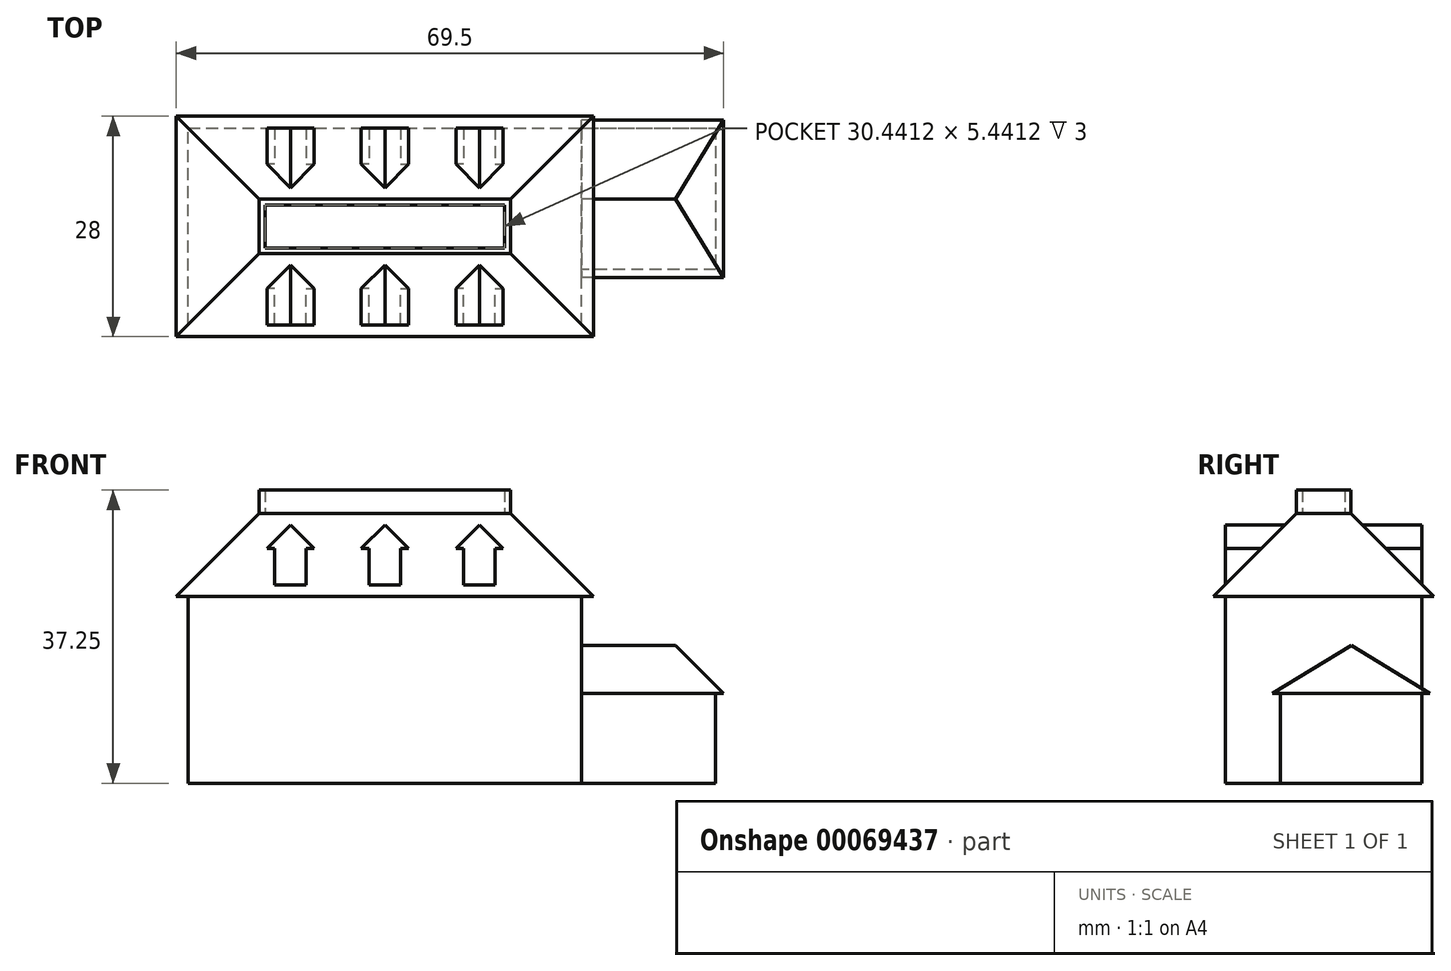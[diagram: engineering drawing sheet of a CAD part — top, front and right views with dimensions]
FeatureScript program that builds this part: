
annotation { "Feature Type Name" : "Feature", "Feature Type Description" : "" }
export const myFeature = defineFeature(function(context is Context, id is Id, definition is map)
    precondition{}
    {
        {
            var Q0;
            Q0=qCreatedBy(makeId("Top.planeOp"),FACE);
            var sketch = newSketch(context, id + "F0", { "sketchPlane" : qUnion([Q0])});
            skLineSegment(sketch, "E0.rect.bottom", {"start": v(25, -12.5) * mm, "end": v(-25, -12.5) * mm});
            skLineSegment(sketch, "E0.rect.top", {"start": v(25, 12.5) * mm, "end": v(-25, 12.5) * mm});
            skLineSegment(sketch, "E0.rect.left", {"start": v(25, -12.5) * mm, "end": v(25, 12.5) * mm, "construction": true});
            skLineSegment(sketch, "E0.rect.right", {"start": v(-25, -12.5) * mm, "end": v(-25, 12.5) * mm});
            skPoint(sketch, "E0.rect.middle", {"position": v(0, 0) * mm});
            skLineSegment(sketch, "E1", {"start": v(25, 12.5) * mm, "end": v(42, 12.5) * mm});
            skLineSegment(sketch, "E2", {"start": v(42, 12.5) * mm, "end": v(42, -5.5) * mm});
            skLineSegment(sketch, "E3", {"start": v(42, -5.5) * mm, "end": v(25, -5.5) * mm});
            skLineSegment(sketch, "E4", {"start": v(25, -12.5) * mm, "end": v(25, -5.5) * mm, "construction": true});
            skLineSegment(sketch, "E5", {"start": v(25, -12.5) * mm, "end": v(25, -5.5) * mm});
            skSolve(sketch);
        }
        {
            var Q0;
            Q0=makeQuery(id+"F0.imprint","IMPRINT",FACE,{"disambiguationData":[TD([[makeQuery(id+"F0.imprint","IMPRINT",EDGE,{"derivedFrom":sQuery(id+"F0.wireOp",EDGE,"E0.rect.bottom")}),-1.0]])]});
            extrude(context, id + "F1", {"entities" : qUnion([Q0]), "depth" : 11.43 * mm});
        }
        {
            var Q0;
            Q0=makeQuery(id+"F1.opExtrude","CAP_FACE",FACE,{"disambiguationData":[OSD([sQuery(id+"F0.wireOp",EDGE,"E0.rect.bottom"),sQuery(id+"F0.wireOp",EDGE,"E0.rect.top"),sQuery(id+"F0.wireOp",EDGE,"E0.rect.right"),sQuery(id+"F0.wireOp",EDGE,"E1"),sQuery(id+"F0.wireOp",EDGE,"E2"),sQuery(id+"F0.wireOp",EDGE,"E3"),sQuery(id+"F0.wireOp",EDGE,"E5")])],"isStart":false});
            var sketch = newSketch(context, id + "F2", { "sketchPlane" : qUnion([Q0])});
            skLineSegment(sketch, "E6.0", {"start": v(25, -12.5) * mm, "end": v(-25, -12.5) * mm});
            skLineSegment(sketch, "E6.1", {"start": v(25, 12.5) * mm, "end": v(-25, 12.5) * mm});
            skLineSegment(sketch, "E6.2", {"start": v(25, -12.5) * mm, "end": v(25, 12.5) * mm});
            skLineSegment(sketch, "E6.3", {"start": v(-25, -12.5) * mm, "end": v(-25, 12.5) * mm});
            skPoint(sketch, "E6.4", {"position": v(0, 0) * mm});
            skLineSegment(sketch, "E6.8", {"start": v(25, -12.5) * mm, "end": v(25, -5.5) * mm});
            skLineSegment(sketch, "E6.9", {"start": v(25, -12.5) * mm, "end": v(25, -5.5) * mm});
            skPoint(sketch, "E6.7.end.orphan", {"position": v(25, -5.5) * mm});
            skPoint(sketch, "E6.7.start.orphan", {"position": v(42, -5.5) * mm});
            skPoint(sketch, "E6.6.end.orphan", {"position": v(42, -5.5) * mm});
            skPoint(sketch, "E6.6.start.orphan", {"position": v(42, 12.5) * mm});
            skPoint(sketch, "E6.5.end.orphan", {"position": v(42, 12.5) * mm});
            skPoint(sketch, "E6.5.start.orphan", {"position": v(25, 12.5) * mm});
            skSolve(sketch);
        }
        {
            var Q0;
            Q0=makeQuery(id+"F2.imprint","IMPRINT",FACE,{"disambiguationData":[TD([[makeQuery(id+"F2.imprint","IMPRINT",EDGE,{"derivedFrom":sQuery(id+"F2.wireOp",EDGE,"E6.0")}),-1.0]])]});
            extrude(context, id + "F3", {"entities" : qUnion([Q0]), "operationType" : NewBodyOperationType.ADD, "depth" : 12.29 * mm});
        }
        {
            var Q0;
            Q0=makeQuery(id+"F3.opExtrude","CAP_FACE",FACE,{"disambiguationData":[OSD([sQuery(id+"F2.wireOp",EDGE,"E6.0"),sQuery(id+"F2.wireOp",EDGE,"E6.1"),sQuery(id+"F2.wireOp",EDGE,"E6.2"),sQuery(id+"F2.wireOp",EDGE,"E6.3"),sQuery(id+"F2.wireOp",EDGE,"E6.9")])],"isStart":false});
            var sketch = newSketch(context, id + "F4", { "sketchPlane" : qUnion([Q0])});
            skLineSegment(sketch, "E7.0", {"start": v(25, -12.5) * mm, "end": v(-25, -12.5) * mm, "construction": true});
            skLineSegment(sketch, "E7.1", {"start": v(25, 12.5) * mm, "end": v(-25, 12.5) * mm, "construction": true});
            skLineSegment(sketch, "E7.2", {"start": v(25, -12.5) * mm, "end": v(25, 12.5) * mm, "construction": true});
            skLineSegment(sketch, "E7.3", {"start": v(-25, -12.5) * mm, "end": v(-25, 12.5) * mm, "construction": true});
            skPoint(sketch, "E7.4", {"position": v(0, 0) * mm});
            skLineSegment(sketch, "E7.5", {"start": v(25, -12.5) * mm, "end": v(25, -5.5) * mm});
            skLineSegment(sketch, "E7.6", {"start": v(25, -12.5) * mm, "end": v(25, -5.5) * mm});
            skPoint(sketch, "E7.7", {"position": v(25, -5.5) * mm});
            skPoint(sketch, "E7.8", {"position": v(42, -5.5) * mm});
            skPoint(sketch, "E7.9", {"position": v(42, -5.5) * mm});
            skPoint(sketch, "E7.10", {"position": v(42, 12.5) * mm});
            skPoint(sketch, "E7.11", {"position": v(42, 12.5) * mm});
            skPoint(sketch, "E7.12", {"position": v(25, 12.5) * mm});
            skLineSegment(sketch, "E8.0", {"start": v(26.5, 14) * mm, "end": v(-26.5, 14) * mm});
            skLineSegment(sketch, "E8.1", {"start": v(26.5, -14) * mm, "end": v(26.5, 14) * mm});
            skLineSegment(sketch, "E8.2", {"start": v(26.5, -14) * mm, "end": v(-26.5, -14) * mm});
            skLineSegment(sketch, "E8.3", {"start": v(-26.5, -14) * mm, "end": v(-26.5, 14) * mm});
            skSolve(sketch);
        }
        {
            var Q0;
            Q0 = qSketchRegion(id + "F4", true);
            var Q1;
            Q1=sQuery(id+"F4.wireOp",EDGE,"E8.0");
            extrude(context, id + "F5", {"entities" : qUnion([Q0]), "operationType" : NewBodyOperationType.ADD, "surfaceEntities" : qUnion([Q1]), "depth" : 10.54 * mm, "hasDraft" : true, "draftAngle" : 45 * degree, "draftPullDirection" : true});
        }
        {
            var Q0;
            Q0=makeQuery(id+"F3.boolean.opBoolean","MERGE",FACE,{"derivedFrom":[makeQuery(id+"F1.opExtrude","SWEPT_FACE",FACE,{"disambiguationData":[OSD([sQuery(id+"F0.wireOp",EDGE,"E0.rect.bottom")])]}),makeQuery(id+"F3.opExtrude","SWEPT_FACE",FACE,{"disambiguationData":[OSD([sQuery(id+"F2.wireOp",EDGE,"E6.0")])]})]});
            var sketch = newSketch(context, id + "F6", { "sketchPlane" : qUnion([Q0])});
            skLineSegment(sketch, "E9", {"start": v(25, 25.22) * mm, "end": v(-25, 25.22) * mm, "construction": true});
            skLineSegment(sketch, "E10", {"start": v(-15, 29.82) * mm, "end": v(-12, 32.82) * mm});
            skLineSegment(sketch, "E11", {"start": v(-12, 32.82) * mm, "end": v(-12, 25.22) * mm, "construction": true});
            skLineSegment(sketch, "E12", {"start": v(-12, 25.22) * mm, "end": v(-14, 25.22) * mm});
            skLineSegment(sketch, "E13", {"start": v(-15, 29.82) * mm, "end": v(-14, 29.82) * mm});
            skLineSegment(sketch, "E14", {"start": v(-14, 29.82) * mm, "end": v(-14, 25.22) * mm});
            skLineSegment(sketch, "E15.MirrorCS", {"start": v(-9, 29.82) * mm, "end": v(-10, 29.82) * mm});
            skLineSegment(sketch, "E16.MirrorCS", {"start": v(-9, 29.82) * mm, "end": v(-12, 32.82) * mm});
            skLineSegment(sketch, "E17.MirrorCS", {"start": v(-10, 29.82) * mm, "end": v(-10, 25.22) * mm});
            skLineSegment(sketch, "E18.MirrorCS", {"start": v(-12, 25.22) * mm, "end": v(-10, 25.22) * mm});
            skLineSegment(sketch, "E19.1.0.0", {"start": v(0, 25.22) * mm, "end": v(2, 25.22) * mm});
            skLineSegment(sketch, "E19.1.0.1", {"start": v(2, 29.82) * mm, "end": v(2, 25.22) * mm});
            skLineSegment(sketch, "E19.1.0.2", {"start": v(-3, 29.82) * mm, "end": v(0, 32.82) * mm});
            skLineSegment(sketch, "E19.1.0.3", {"start": v(3, 29.82) * mm, "end": v(0, 32.82) * mm});
            skLineSegment(sketch, "E19.1.0.4", {"start": v(0, 32.82) * mm, "end": v(0, 25.22) * mm, "construction": true});
            skLineSegment(sketch, "E19.1.0.5", {"start": v(0, 25.22) * mm, "end": v(-2, 25.22) * mm});
            skLineSegment(sketch, "E19.1.0.6", {"start": v(-2, 29.82) * mm, "end": v(-2, 25.22) * mm});
            skLineSegment(sketch, "E19.1.0.7", {"start": v(3, 29.82) * mm, "end": v(2, 29.82) * mm});
            skLineSegment(sketch, "E19.1.0.8", {"start": v(-3, 29.82) * mm, "end": v(-2, 29.82) * mm});
            skLineSegment(sketch, "E19.2.0.0", {"start": v(12, 25.22) * mm, "end": v(14, 25.22) * mm});
            skLineSegment(sketch, "E19.2.0.1", {"start": v(14, 29.82) * mm, "end": v(14, 25.22) * mm});
            skLineSegment(sketch, "E19.2.0.2", {"start": v(9, 29.82) * mm, "end": v(12, 32.82) * mm});
            skLineSegment(sketch, "E19.2.0.3", {"start": v(15, 29.82) * mm, "end": v(12, 32.82) * mm});
            skLineSegment(sketch, "E19.2.0.4", {"start": v(12, 32.82) * mm, "end": v(12, 25.22) * mm, "construction": true});
            skLineSegment(sketch, "E19.2.0.5", {"start": v(12, 25.22) * mm, "end": v(10, 25.22) * mm});
            skLineSegment(sketch, "E19.2.0.6", {"start": v(10, 29.82) * mm, "end": v(10, 25.22) * mm});
            skLineSegment(sketch, "E19.2.0.7", {"start": v(15, 29.82) * mm, "end": v(14, 29.82) * mm});
            skLineSegment(sketch, "E19.2.0.8", {"start": v(9, 29.82) * mm, "end": v(10, 29.82) * mm});
            skLineSegment(sketch, "E19.direction1", {"start": v(-12, 25.22) * mm, "end": v(0, 25.22) * mm, "construction": true});
            skSolve(sketch);
        }
        {
            var Q0;
            Q0=makeQuery(id+"F6.imprint","IMPRINT",FACE,{"disambiguationData":[TD([[makeQuery(id+"F6.imprint","IMPRINT",EDGE,{"derivedFrom":sQuery(id+"F6.wireOp",EDGE,"E10")}),-1.0]])]});
            var Q1;
            Q1=makeQuery(id+"F6.imprint","IMPRINT",FACE,{"disambiguationData":[TD([[makeQuery(id+"F6.imprint","IMPRINT",EDGE,{"derivedFrom":sQuery(id+"F6.wireOp",EDGE,"E19.1.0.0")}),1.0]])]});
            var Q2;
            Q2=makeQuery(id+"F6.imprint","IMPRINT",FACE,{"disambiguationData":[TD([[makeQuery(id+"F6.imprint","IMPRINT",EDGE,{"derivedFrom":sQuery(id+"F6.wireOp",EDGE,"E19.2.0.0")}),1.0]])]});
            var Q3;
            Q3=makeQuery(id+"F1.opExtrude","SWEPT_BODY",BODY,{"disambiguationData":[OSD([sQuery(id+"F0.wireOp",EDGE,"E0.rect.bottom"),sQuery(id+"F0.wireOp",EDGE,"E0.rect.top"),sQuery(id+"F0.wireOp",EDGE,"E0.rect.right"),sQuery(id+"F0.wireOp",EDGE,"E1"),sQuery(id+"F0.wireOp",EDGE,"E2"),sQuery(id+"F0.wireOp",EDGE,"E3"),sQuery(id+"F0.wireOp",EDGE,"E5")])]});
            extrude(context, id + "F7", {"entities" : qUnion([Q0, Q1, Q2]), "endBound" : BoundingType.UP_TO_BODY, "oppositeDirection" : true, "endBoundEntityBody" : qUnion([Q3]), "depth" : 25 * mm});
        }
        {
            var Q0;
            Q0=makeQuery(id+"F7.opExtrude","SWEPT_BODY",BODY,{"disambiguationData":[OSD([sQuery(id+"F6.wireOp",EDGE,"E10"),sQuery(id+"F6.wireOp",EDGE,"E12"),sQuery(id+"F6.wireOp",EDGE,"E13"),sQuery(id+"F6.wireOp",EDGE,"E14"),sQuery(id+"F6.wireOp",EDGE,"E15.MirrorCS"),sQuery(id+"F6.wireOp",EDGE,"E16.MirrorCS"),sQuery(id+"F6.wireOp",EDGE,"E17.MirrorCS"),sQuery(id+"F6.wireOp",EDGE,"E18.MirrorCS")])]});
            var Q1;
            Q1=makeQuery(id+"F7.opExtrude","SWEPT_BODY",BODY,{"disambiguationData":[OSD([sQuery(id+"F6.wireOp",EDGE,"E19.1.0.0"),sQuery(id+"F6.wireOp",EDGE,"E19.1.0.1"),sQuery(id+"F6.wireOp",EDGE,"E19.1.0.2"),sQuery(id+"F6.wireOp",EDGE,"E19.1.0.3"),sQuery(id+"F6.wireOp",EDGE,"E19.1.0.5"),sQuery(id+"F6.wireOp",EDGE,"E19.1.0.6"),sQuery(id+"F6.wireOp",EDGE,"E19.1.0.7"),sQuery(id+"F6.wireOp",EDGE,"E19.1.0.8")])]});
            var Q2;
            Q2=makeQuery(id+"F7.opExtrude","SWEPT_BODY",BODY,{"disambiguationData":[OSD([sQuery(id+"F6.wireOp",EDGE,"E19.2.0.0"),sQuery(id+"F6.wireOp",EDGE,"E19.2.0.1"),sQuery(id+"F6.wireOp",EDGE,"E19.2.0.2"),sQuery(id+"F6.wireOp",EDGE,"E19.2.0.3"),sQuery(id+"F6.wireOp",EDGE,"E19.2.0.5"),sQuery(id+"F6.wireOp",EDGE,"E19.2.0.6"),sQuery(id+"F6.wireOp",EDGE,"E19.2.0.7"),sQuery(id+"F6.wireOp",EDGE,"E19.2.0.8")])]});
            var Q3;
            Q3=qCreatedBy(makeId("Front.planeOp"),FACE);
            mirror(context, id + "F8", {"operationType" : NewBodyOperationType.ADD, "entities" : qUnion([Q0, Q1, Q2]), "mirrorPlane" : qUnion([Q3])});
        }
        {
            var Q0;
            Q0=makeQuery(id+"F3.boolean.opBoolean","MERGE",FACE,{"derivedFrom":[makeQuery(id+"F1.opExtrude","SWEPT_FACE",FACE,{"disambiguationData":[OSD([sQuery(id+"F0.wireOp",EDGE,"E5")])]}),makeQuery(id+"F3.opExtrude","SWEPT_FACE",FACE,{"disambiguationData":[OSD([sQuery(id+"F2.wireOp",EDGE,"E6.2"),sQuery(id+"F2.wireOp",EDGE,"E6.9")])]})]});
            var sketch = newSketch(context, id + "F9", { "sketchPlane" : qUnion([Q0])});
            skLineSegment(sketch, "E20", {"start": v(-6.5, 11.43) * mm, "end": v(13.5, 11.43) * mm});
            skLineSegment(sketch, "E21", {"start": v(13.5, 11.43) * mm, "end": v(3.5, 17.5) * mm});
            skLineSegment(sketch, "E22", {"start": v(3.5, 17.5) * mm, "end": v(-6.5, 11.43) * mm});
            skPoint(sketch, "E23", {"position": v(3.5, 11.43) * mm});
            skSolve(sketch);
        }
        {
            var Q0;
            {var subQ0=sQuery(id+"F9.wireOp",EDGE,"E22");Q0=makeQuery(id+"F9.imprint","IMPRINT",FACE,{"disambiguationData":[TD([[makeQuery(id+"F9.imprint","IMPRINT",EDGE,{"derivedFrom":subQ0}),1.0]])]});}
            var Q1;
            {var subQ0=sQuery(id+"F9.wireOp",EDGE,"E20");var subQ3=sQuery(id+"F9.wireOp",EDGE,"E21");var subQ4=makeQuery(id+"F9.imprint","INTERSECT",VERTEX,{"derivedFrom":[subQ0,subQ3]});Q1=makeQuery(id+"F9.imprint","IMPRINT",FACE,{"disambiguationData":[TD([[makeQuery(id+"F9.imprint","IMPRINT",EDGE,{"disambiguationData":[TD([[subQ4,1.0]])],"derivedFrom":subQ0}),1.0]])]});}
            extrude(context, id + "F10", {"entities" : qUnion([Q0, Q1]), "operationType" : NewBodyOperationType.ADD, "depth" : 18 * mm});
        }
        {
            var Q0;
            Q0=makeQuery(id+"F1.opExtrude","SWEPT_FACE",FACE,{"disambiguationData":[OSD([sQuery(id+"F0.wireOp",EDGE,"E3")])]});
            var sketch = newSketch(context, id + "F11", { "sketchPlane" : qUnion([Q0])});
            skLineSegment(sketch, "E24", {"start": v(43, 17.5) * mm, "end": v(36.94, 17.5) * mm});
            skLineSegment(sketch, "E25", {"start": v(36.94, 17.5) * mm, "end": v(43, 11.43) * mm});
            skLineSegment(sketch, "E26", {"start": v(43, 11.43) * mm, "end": v(43, 17.5) * mm});
            skSolve(sketch);
        }
        {
            var Q0;
            Q0=makeQuery(id+"F11.imprint","IMPRINT",FACE,{"disambiguationData":[TD([[makeQuery(id+"F11.imprint","IMPRINT",EDGE,{"derivedFrom":sQuery(id+"F11.wireOp",EDGE,"E24")}),1.0]])]});
            extrude(context, id + "F12", {"entities" : qUnion([Q0]), "operationType" : NewBodyOperationType.REMOVE, "endBound" : BoundingType.THROUGH_ALL, "oppositeDirection" : true, "depth" : 25 * mm, "hasSecondDirection" : true, "secondDirectionBound" : SecondDirectionBoundingType.THROUGH_ALL, "secondDirectionOppositeDirection" : false, "secondDirectionDepth" : 25 * mm});
        }
        {
            var Q0;
            Q0=makeQuery(id+"F5.opExtrude","CAP_FACE",FACE,{"disambiguationData":[OSD([sQuery(id+"F4.wireOp",EDGE,"E8.0"),sQuery(id+"F4.wireOp",EDGE,"E8.1"),sQuery(id+"F4.wireOp",EDGE,"E8.2"),sQuery(id+"F4.wireOp",EDGE,"E8.3")])],"isStart":false});
            var sketch = newSketch(context, id + "F13", { "sketchPlane" : qUnion([Q0])});
            skLineSegment(sketch, "E27.bottom", {"start": v(-15.96, 3.46) * mm, "end": v(15.96, 3.46) * mm});
            skLineSegment(sketch, "E27.top", {"start": v(-15.96, -3.46) * mm, "end": v(15.96, -3.46) * mm});
            skLineSegment(sketch, "E27.left", {"start": v(-15.96, 3.46) * mm, "end": v(-15.96, -3.46) * mm});
            skLineSegment(sketch, "E27.right", {"start": v(15.96, 3.46) * mm, "end": v(15.96, -3.46) * mm});
            skLineSegment(sketch, "E28.0", {"start": v(-15.22, 2.72) * mm, "end": v(15.22, 2.72) * mm});
            skLineSegment(sketch, "E28.1", {"start": v(-15.22, 2.72) * mm, "end": v(-15.22, -2.72) * mm});
            skLineSegment(sketch, "E28.2", {"start": v(-15.22, -2.72) * mm, "end": v(15.22, -2.72) * mm});
            skLineSegment(sketch, "E28.3", {"start": v(15.22, 2.72) * mm, "end": v(15.22, -2.72) * mm});
            skSolve(sketch);
        }
        {
            var Q0;
            Q0=makeQuery(id+"F13.imprint","IMPRINT",FACE,{"disambiguationData":[TD([[makeQuery(id+"F13.imprint","IMPRINT",EDGE,{"derivedFrom":sQuery(id+"F13.wireOp",EDGE,"E27.bottom")}),1.0]])]});
            extrude(context, id + "F14", {"entities" : qUnion([Q0]), "operationType" : NewBodyOperationType.ADD, "depth" : 3 * mm});
        }
    });
